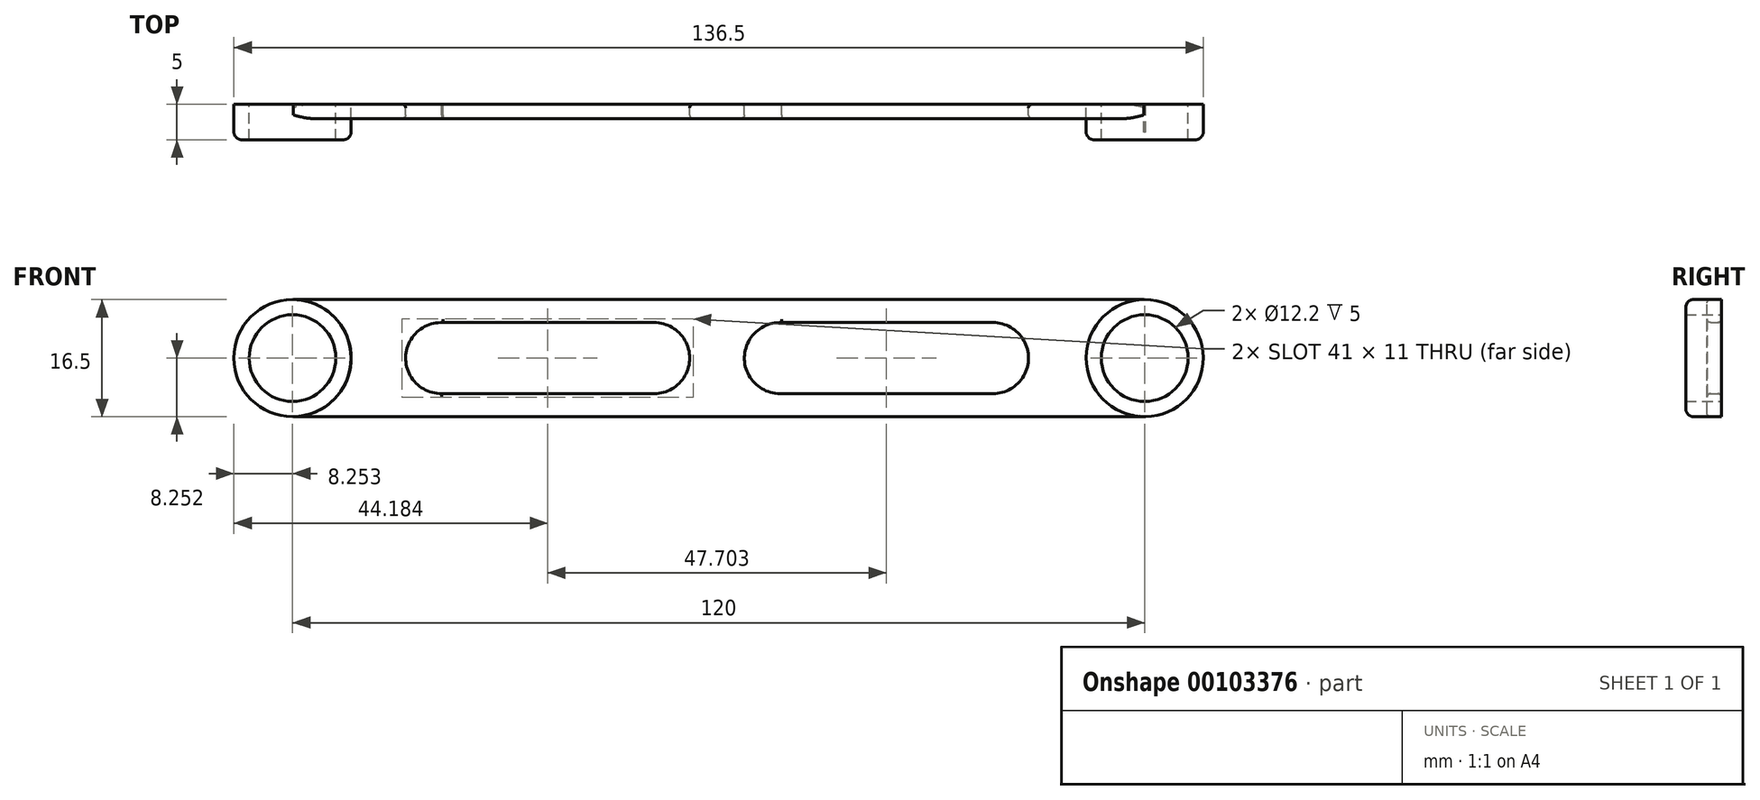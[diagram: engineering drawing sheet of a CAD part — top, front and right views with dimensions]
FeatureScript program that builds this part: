
annotation { "Feature Type Name" : "Feature", "Feature Type Description" : "" }
export const myFeature = defineFeature(function(context is Context, id is Id, definition is map)
    precondition{}
    {
        {
            var Q0;
            Q0=qCreatedBy(makeId("Front.planeOp"),FACE);
            var sketch = newSketch(context, id + "F0", { "sketchPlane" : qUnion([Q0])});
            skCircle(sketch, "E0", {"center": v(-42.99, -0.05) * mm, "radius": 6.1 * mm});
            skCircle(sketch, "E1", {"center": v(-42.99, -0.05) * mm, "radius": 8.25 * mm});
            skCircle(sketch, "E2", {"center": v(77.01, -0.05) * mm, "radius": 6.1 * mm});
            skCircle(sketch, "E3", {"center": v(77.01, -0.05) * mm, "radius": 8.25 * mm});
            skLineSegment(sketch, "E4.bottom", {"start": v(-42.88, 8.2) * mm, "end": v(76.9, 8.2) * mm});
            skLineSegment(sketch, "E4.top", {"start": v(-42.88, -8.3) * mm, "end": v(77.12, -8.3) * mm});
            skCircle(sketch, "E5", {"center": v(-22.06, -0.05) * mm, "radius": 5 * mm});
            skCircle(sketch, "E6", {"center": v(7.94, -0.05) * mm, "radius": 5 * mm});
            skLineSegment(sketch, "E7", {"start": v(-21.8, 4.95) * mm, "end": v(7.94, 4.95) * mm});
            skLineSegment(sketch, "E8", {"start": v(-22.13, -5.05) * mm, "end": v(7.94, -5.05) * mm});
            skCircle(sketch, "E9", {"center": v(25.65, -0.05) * mm, "radius": 5 * mm});
            skCircle(sketch, "E10", {"center": v(55.65, -0.05) * mm, "radius": 5 * mm});
            skLineSegment(sketch, "E11", {"start": v(25.9, 4.95) * mm, "end": v(55.64, 4.95) * mm});
            skLineSegment(sketch, "E12", {"start": v(25.65, -5.05) * mm, "end": v(55.65, -5.05) * mm});
            skSolve(sketch);
        }
        {
            var Q0;
            Q0=makeQuery(id+"F0.imprint","IMPRINT",FACE,{"disambiguationData":[TD([[makeQuery(id+"F0.imprint","IMPRINT",EDGE,{"derivedFrom":sQuery(id+"F0.wireOp",EDGE,"E0")}),-1.0]])]});
            var Q1;
            Q1=makeQuery(id+"F0.imprint","IMPRINT",FACE,{"disambiguationData":[TD([[makeQuery(id+"F0.imprint","IMPRINT",EDGE,{"derivedFrom":sQuery(id+"F0.wireOp",EDGE,"E2")}),-1.0]])]});
            extrude(context, id + "F1", {"entities" : qUnion([Q0, Q1]), "depth" : 5 * mm});
        }
        {
            var Q0;
            {var subQ0=sQuery(id+"F0.wireOp",EDGE,"E4.bottom");Q0=makeQuery(id+"F0.imprint","IMPRINT",FACE,{"disambiguationData":[TD([[makeQuery(id+"F0.imprint","IMPRINT",EDGE,{"derivedFrom":subQ0}),-1.0]])]});}
            extrude(context, id + "F2", {"entities" : qUnion([Q0]), "depth" : 2 * mm});
        }
        {
            var Q0;
            Q0=makeQuery(id+"F1.opExtrude","CAP_EDGE",EDGE,{"disambiguationData":[OSD([sQuery(id+"F0.wireOp",EDGE,"E1")])],"isStart":false});
            fillet(context, id + "F3", {"entities" : qUnion([Q0]), "radius" : 1.1 * mm, "tangentPropagation" : true, "allowEdgeOverflow" : false});
        }
        {
            var Q0;
            Q0=makeQuery(id+"F1.opExtrude","CAP_EDGE",EDGE,{"disambiguationData":[OSD([sQuery(id+"F0.wireOp",EDGE,"E3")])],"isStart":false});
            fillet(context, id + "F4", {"entities" : qUnion([Q0]), "radius" : 1.1 * mm, "tangentPropagation" : true, "allowEdgeOverflow" : false});
        }
        {
            var Q0;
            Q0=makeQuery(id+"F2.opExtrude","CAP_EDGE",EDGE,{"disambiguationData":[OSD([sQuery(id+"F0.wireOp",EDGE,"E4.top")])],"isStart":false});
            var Q1;
            Q1=makeQuery(id+"F2.opExtrude","CAP_EDGE",EDGE,{"disambiguationData":[OSD([sQuery(id+"F0.wireOp",EDGE,"E4.bottom")])],"isStart":false});
            var Q2;
            Q2=makeQuery(id+"F2.opExtrude","CAP_EDGE",EDGE,{"disambiguationData":[OSD([sQuery(id+"F0.wireOp",EDGE,"E4.top")])],"isStart":true});
            fillet(context, id + "F5", {"entities" : qUnion([Q0, Q1, Q2]), "radius" : .5 * mm, "tangentPropagation" : true, "allowEdgeOverflow" : false});
        }
        {
            var Q0;
            {var subQ0=sQuery(id+"F0.wireOp",EDGE,"E5");var subQ1=makeQuery(id+"F0.imprint","INTERSECT",VERTEX,{"derivedFrom":[subQ0,sQuery(id+"F0.wireOp",EDGE,"E7")]});Q0=makeQuery(id+"F0.imprint","IMPRINT",FACE,{"disambiguationData":[TD([[makeQuery(id+"F0.imprint","IMPRINT",EDGE,{"disambiguationData":[TD([[subQ1,-1.0]])],"derivedFrom":subQ0}),1.0]])]});}
            var Q1;
            {var subQ0=sQuery(id+"F0.wireOp",EDGE,"E7");Q1=makeQuery(id+"F0.imprint","IMPRINT",FACE,{"disambiguationData":[TD([[makeQuery(id+"F0.imprint","IMPRINT",EDGE,{"derivedFrom":subQ0}),-1.0]])]});}
            var Q2;
            {var subQ0=sQuery(id+"F0.wireOp",EDGE,"E6");var subQ1=makeQuery(id+"F0.imprint","INTERSECT",VERTEX,{"derivedFrom":[subQ0,sQuery(id+"F0.wireOp",EDGE,"E7")]});Q2=makeQuery(id+"F0.imprint","IMPRINT",FACE,{"disambiguationData":[TD([[makeQuery(id+"F0.imprint","IMPRINT",EDGE,{"disambiguationData":[TD([[subQ1,-1.0]])],"derivedFrom":subQ0}),1.0]])]});}
            extrude(context, id + "F6", {"entities" : qUnion([Q0, Q1, Q2]), "operationType" : NewBodyOperationType.REMOVE, "oppositeDirection" : true, "depth" : 10 * mm});
        }
        {
            var Q0;
            Q0=makeQuery(id+"F2.opExtrude","CAP_EDGE",EDGE,{"disambiguationData":[OSD([sQuery(id+"F0.wireOp",EDGE,"E6")])],"isStart":false});
            var Q1;
            Q1=makeQuery(id+"F2.opExtrude","CAP_EDGE",EDGE,{"disambiguationData":[OSD([sQuery(id+"F0.wireOp",EDGE,"E7")])],"isStart":false});
            var Q2;
            Q2=makeQuery(id+"F2.opExtrude","CAP_EDGE",EDGE,{"disambiguationData":[OSD([sQuery(id+"F0.wireOp",EDGE,"E5")])],"isStart":false});
            var Q3;
            Q3=makeQuery(id+"F2.opExtrude","CAP_EDGE",EDGE,{"disambiguationData":[OSD([sQuery(id+"F0.wireOp",EDGE,"E8")])],"isStart":false});
            var Q4;
            Q4=makeQuery(id+"F2.opExtrude","CAP_EDGE",EDGE,{"disambiguationData":[OSD([sQuery(id+"F0.wireOp",EDGE,"E12")])],"isStart":false});
            var Q5;
            Q5=makeQuery(id+"F2.opExtrude","CAP_EDGE",EDGE,{"disambiguationData":[OSD([sQuery(id+"F0.wireOp",EDGE,"E9")])],"isStart":false});
            var Q6;
            Q6=makeQuery(id+"F2.opExtrude","CAP_EDGE",EDGE,{"disambiguationData":[OSD([sQuery(id+"F0.wireOp",EDGE,"E11")])],"isStart":false});
            var Q7;
            Q7=makeQuery(id+"F2.opExtrude","CAP_EDGE",EDGE,{"disambiguationData":[OSD([sQuery(id+"F0.wireOp",EDGE,"E10")])],"isStart":false});
            var Q8;
            Q8=makeQuery(id+"F2.opExtrude","CAP_EDGE",EDGE,{"disambiguationData":[OSD([sQuery(id+"F0.wireOp",EDGE,"E6")])],"isStart":true});
            var Q9;
            Q9=makeQuery(id+"F2.opExtrude","CAP_EDGE",EDGE,{"disambiguationData":[OSD([sQuery(id+"F0.wireOp",EDGE,"E8")])],"isStart":true});
            var Q10;
            {var subQ0=sQuery(id+"F0.wireOp",EDGE,"E7");var subQ1=sQuery(id+"F0.wireOp",EDGE,"E5");Q10=makeQuery(id+"F6.boolean.opBoolean","SPLIT",EDGE,{"disambiguationData":[TD([makeQuery(id+"F2.opExtrude","SWEPT_FACE",FACE,{"disambiguationData":[OSD([subQ0])]})])],"derivedFrom":makeQuery(id+"F2.opExtrude","CAP_EDGE",EDGE,{"disambiguationData":[OSD([subQ1])],"isStart":true})});}
            var Q11;
            Q11=makeQuery(id+"F2.opExtrude","CAP_EDGE",EDGE,{"disambiguationData":[OSD([sQuery(id+"F0.wireOp",EDGE,"E7")])],"isStart":true});
            var Q12;
            Q12=makeQuery(id+"F2.opExtrude","CAP_EDGE",EDGE,{"disambiguationData":[OSD([sQuery(id+"F0.wireOp",EDGE,"E11")])],"isStart":true});
            var Q13;
            Q13=makeQuery(id+"F2.opExtrude","CAP_EDGE",EDGE,{"disambiguationData":[OSD([sQuery(id+"F0.wireOp",EDGE,"E9")])],"isStart":true});
            var Q14;
            Q14=makeQuery(id+"F2.opExtrude","CAP_EDGE",EDGE,{"disambiguationData":[OSD([sQuery(id+"F0.wireOp",EDGE,"E12")])],"isStart":true});
            var Q15;
            Q15=makeQuery(id+"F2.opExtrude","CAP_EDGE",EDGE,{"disambiguationData":[OSD([sQuery(id+"F0.wireOp",EDGE,"E10")])],"isStart":true});
            fillet(context, id + "F7", {"entities" : qUnion([Q0, Q1, Q2, Q3, Q4, Q5, Q6, Q7, Q8, Q9, Q10, Q11, Q12, Q13, Q14, Q15]), "radius" : .5 * mm, "tangentPropagation" : true, "allowEdgeOverflow" : false});
        }
    });
